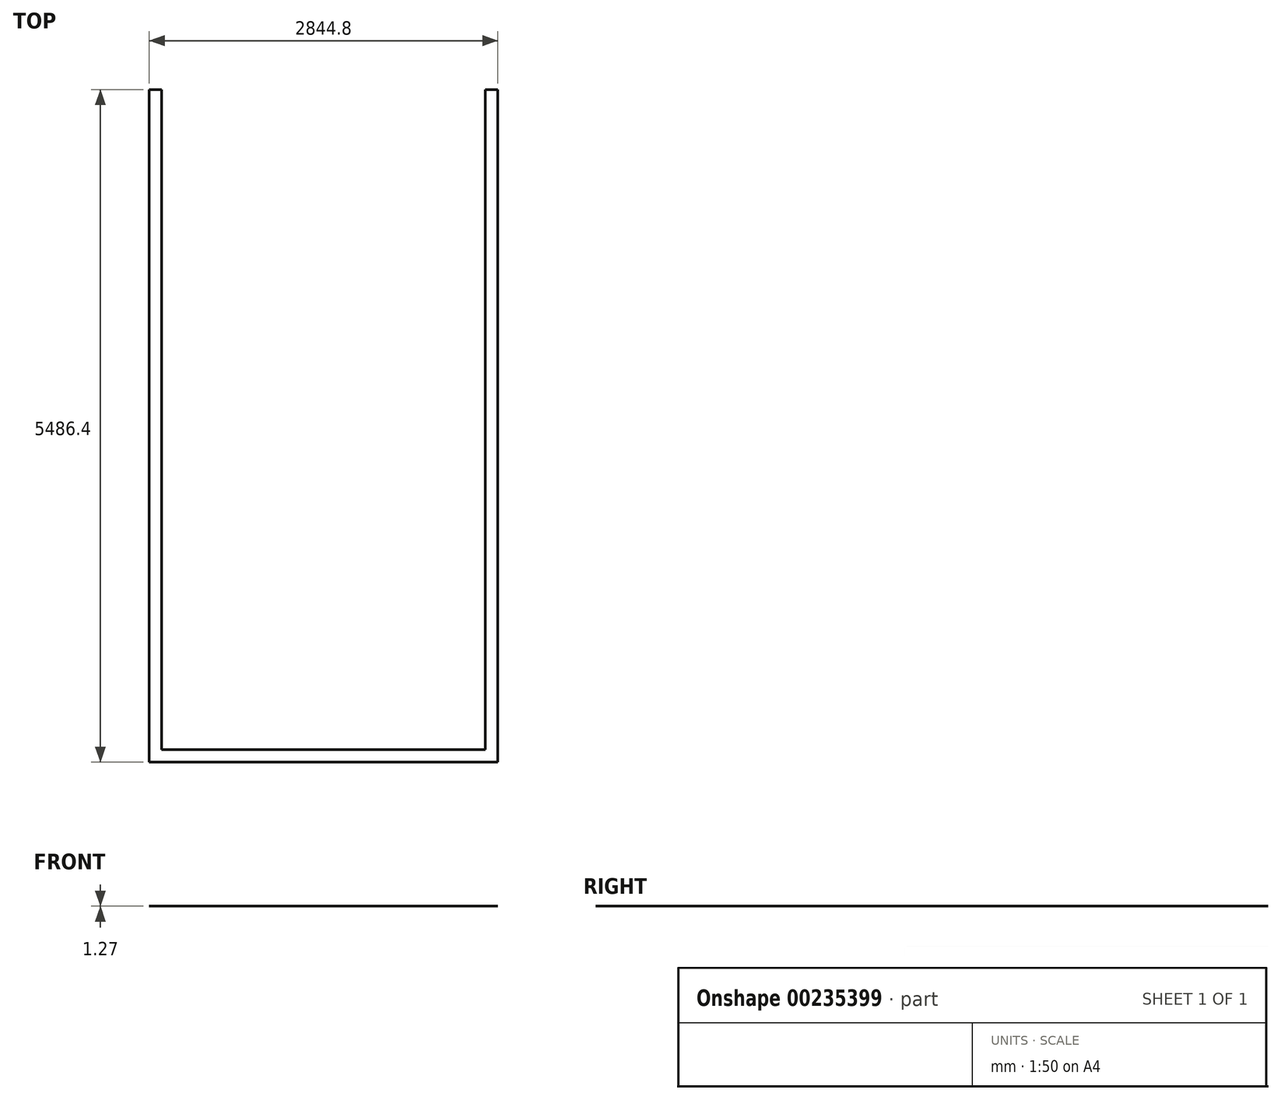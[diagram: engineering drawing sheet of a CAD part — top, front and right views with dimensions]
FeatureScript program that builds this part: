
annotation { "Feature Type Name" : "Feature", "Feature Type Description" : "" }
export const myFeature = defineFeature(function(context is Context, id is Id, definition is map)
    precondition{}
    {
        {
            var Q0;
            Q0=qCreatedBy(makeId("Top.planeOp"),FACE);
            var sketch = newSketch(context, id + "F0", { "sketchPlane" : qUnion([Q0])});
            skLineSegment(sketch, "E0", {"start": v(0, 0) * mm, "end": v(0, 5486.4) * mm});
            skLineSegment(sketch, "E1", {"start": v(0, 5486.4) * mm, "end": v(101.6, 5486.4) * mm});
            skLineSegment(sketch, "E2", {"start": v(101.6, 5486.4) * mm, "end": v(101.6, 101.6) * mm});
            skLineSegment(sketch, "E3", {"start": v(101.6, 101.6) * mm, "end": v(2743.2, 101.6) * mm});
            skLineSegment(sketch, "E4", {"start": v(2743.2, 101.6) * mm, "end": v(2743.2, 5486.4) * mm});
            skLineSegment(sketch, "E5", {"start": v(2743.2, 5486.4) * mm, "end": v(2844.8, 5486.4) * mm});
            skLineSegment(sketch, "E6", {"start": v(2844.8, 5486.4) * mm, "end": v(2844.8, 0) * mm});
            skLineSegment(sketch, "E7", {"start": v(2844.8, 0) * mm, "end": v(0, 0) * mm});
            skSolve(sketch);
        }
        {
            var Q0;
            Q0 = qSketchRegion(id + "F0", true);
            extrude(context, id + "F1", {"entities" : qUnion([Q0]), "depth" : 1.27 * mm});
        }
    });
